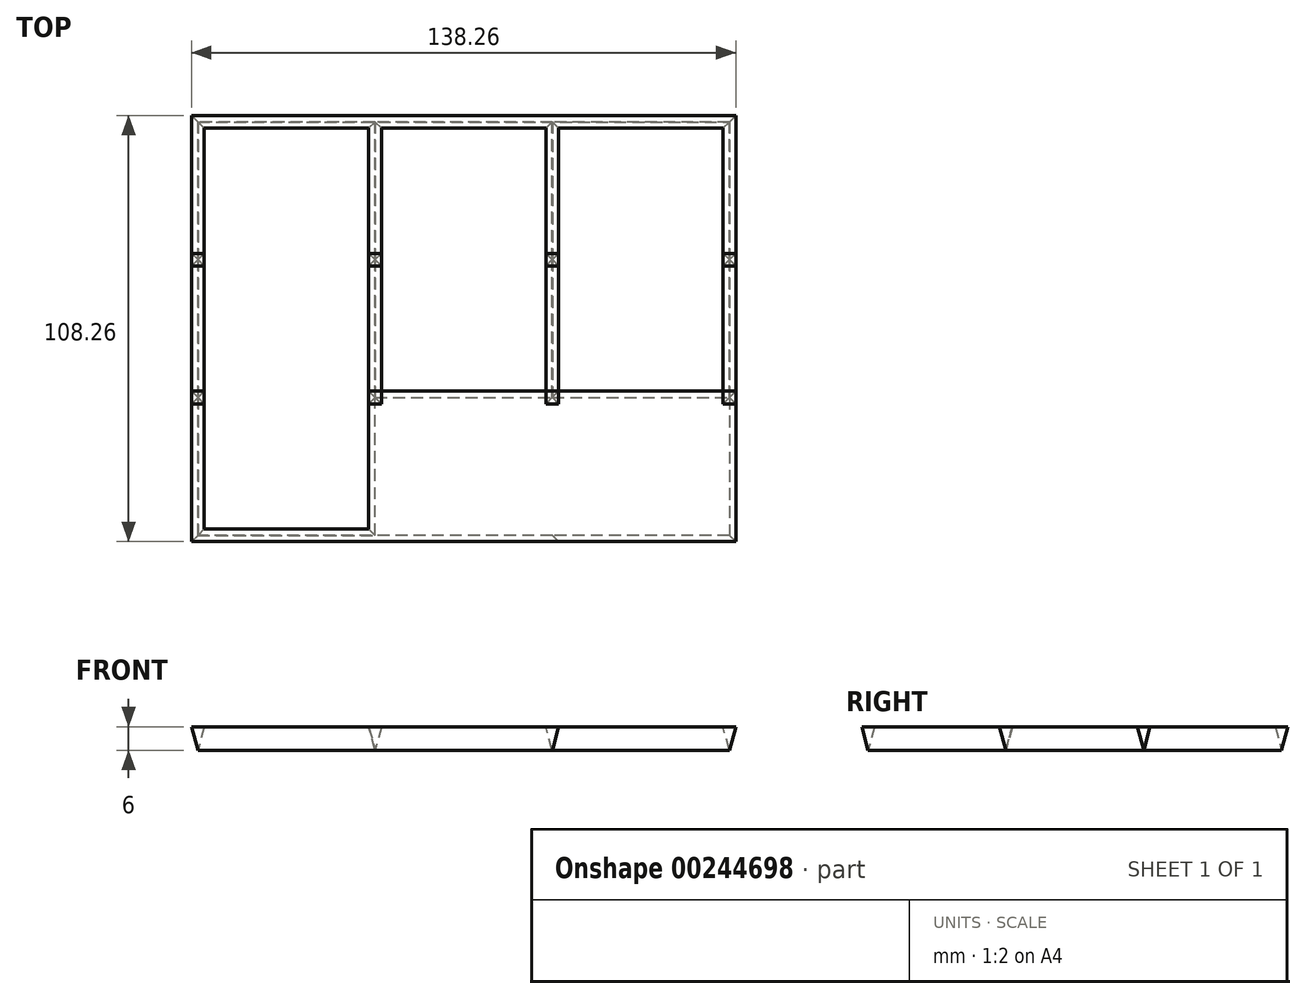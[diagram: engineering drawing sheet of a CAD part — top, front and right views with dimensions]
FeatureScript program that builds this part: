
annotation { "Feature Type Name" : "Feature", "Feature Type Description" : "" }
export const myFeature = defineFeature(function(context is Context, id is Id, definition is map)
    precondition{}
    {
        {
            var Q0;
            Q0=qCreatedBy(makeId("Top.planeOp"),FACE);
            var sketch = newSketch(context, id + "F0", { "sketchPlane" : qUnion([Q0])});
            skLineSegment(sketch, "E0.bottom", {"start": v(0, 0) * mm, "end": v(45, 0) * mm});
            skLineSegment(sketch, "E0.top", {"start": v(0, 35) * mm, "end": v(45, 35) * mm});
            skLineSegment(sketch, "E0.left", {"start": v(0, 0) * mm, "end": v(0, 35) * mm});
            skLineSegment(sketch, "E0.right", {"start": v(45, 0) * mm, "end": v(45, 35) * mm});
            skLineSegment(sketch, "E1.0", {"start": v(-0.01, 35.01) * mm, "end": v(45, 35.01) * mm});
            skLineSegment(sketch, "E1.1", {"start": v(-0.01, -0.01) * mm, "end": v(-0.01, 35.01) * mm});
            skLineSegment(sketch, "E1.2", {"start": v(-0.01, -0.01) * mm, "end": v(45, -0.01) * mm});
            skLineSegment(sketch, "E1.3", {"start": v(45, -0.01) * mm, "end": v(45, 35.01) * mm});
            skLineSegment(sketch, "E2.0.1.0", {"start": v(45, 35) * mm, "end": v(45, 70.02) * mm});
            skLineSegment(sketch, "E2.0.1.1", {"start": v(-0.01, 35) * mm, "end": v(45, 35) * mm});
            skLineSegment(sketch, "E2.0.1.2", {"start": v(-0.01, 35) * mm, "end": v(-0.01, 70.02) * mm});
            skLineSegment(sketch, "E2.0.1.3", {"start": v(-0.01, 70.02) * mm, "end": v(45, 70.02) * mm});
            skLineSegment(sketch, "E2.0.1.4", {"start": v(0, 70.01) * mm, "end": v(45, 70.01) * mm});
            skLineSegment(sketch, "E2.0.1.5", {"start": v(45, 35) * mm, "end": v(45, 70.01) * mm});
            skLineSegment(sketch, "E2.0.1.6", {"start": v(0, 35) * mm, "end": v(0, 70.01) * mm});
            skLineSegment(sketch, "E2.0.2.0", {"start": v(45, 70) * mm, "end": v(45, 105.03) * mm});
            skLineSegment(sketch, "E2.0.2.1", {"start": v(-0.01, 70) * mm, "end": v(45, 70) * mm});
            skLineSegment(sketch, "E2.0.2.2", {"start": v(-0.01, 70) * mm, "end": v(-0.01, 105.03) * mm});
            skLineSegment(sketch, "E2.0.2.3", {"start": v(-0.01, 105.03) * mm, "end": v(45, 105.03) * mm});
            skLineSegment(sketch, "E2.0.2.4", {"start": v(0, 105.02) * mm, "end": v(45, 105.02) * mm});
            skLineSegment(sketch, "E2.0.2.5", {"start": v(45, 70.02) * mm, "end": v(45, 105.02) * mm});
            skLineSegment(sketch, "E2.0.2.6", {"start": v(0, 70.02) * mm, "end": v(0, 105.02) * mm});
            skLineSegment(sketch, "E2.0.2.7", {"start": v(0, 70.02) * mm, "end": v(45, 70.02) * mm});
            skLineSegment(sketch, "E2.1.0.0", {"start": v(90.02, -0.01) * mm, "end": v(90.02, 35.01) * mm});
            skLineSegment(sketch, "E2.1.0.1", {"start": v(45, -0.01) * mm, "end": v(90.02, -0.01) * mm});
            skLineSegment(sketch, "E2.1.0.3", {"start": v(45, 35.01) * mm, "end": v(90.02, 35.01) * mm});
            skLineSegment(sketch, "E2.1.0.4", {"start": v(45, 35) * mm, "end": v(90.01, 35) * mm});
            skLineSegment(sketch, "E2.1.0.5", {"start": v(90.01, 0) * mm, "end": v(90.01, 35) * mm});
            skLineSegment(sketch, "E2.1.0.7", {"start": v(45, 0) * mm, "end": v(90.01, 0) * mm});
            skLineSegment(sketch, "E2.1.1.0", {"start": v(90.02, 35) * mm, "end": v(90.02, 70.02) * mm});
            skLineSegment(sketch, "E2.1.1.1", {"start": v(45, 35) * mm, "end": v(90.02, 35) * mm});
            skLineSegment(sketch, "E2.1.1.2", {"start": v(45, 35) * mm, "end": v(45, 70.02) * mm});
            skLineSegment(sketch, "E2.1.1.3", {"start": v(45, 70.02) * mm, "end": v(90.02, 70.02) * mm});
            skLineSegment(sketch, "E2.1.1.4", {"start": v(45, 70.01) * mm, "end": v(90.01, 70.01) * mm});
            skLineSegment(sketch, "E2.1.1.5", {"start": v(90.01, 35) * mm, "end": v(90.01, 70.01) * mm});
            skLineSegment(sketch, "E2.1.1.6", {"start": v(45, 35) * mm, "end": v(45, 70.01) * mm});
            skLineSegment(sketch, "E2.1.1.7", {"start": v(45, 35) * mm, "end": v(90.01, 35) * mm});
            skLineSegment(sketch, "E2.1.2.0", {"start": v(90.02, 70) * mm, "end": v(90.02, 105.03) * mm});
            skLineSegment(sketch, "E2.1.2.1", {"start": v(45, 70) * mm, "end": v(90.02, 70) * mm});
            skLineSegment(sketch, "E2.1.2.2", {"start": v(45, 70) * mm, "end": v(45, 105.03) * mm});
            skLineSegment(sketch, "E2.1.2.3", {"start": v(45, 105.03) * mm, "end": v(90.02, 105.03) * mm});
            skLineSegment(sketch, "E2.1.2.4", {"start": v(45, 105.02) * mm, "end": v(90.01, 105.02) * mm});
            skLineSegment(sketch, "E2.1.2.5", {"start": v(90.01, 70.02) * mm, "end": v(90.01, 105.02) * mm});
            skLineSegment(sketch, "E2.1.2.6", {"start": v(45, 70.02) * mm, "end": v(45, 105.02) * mm});
            skLineSegment(sketch, "E2.1.2.7", {"start": v(45, 70.02) * mm, "end": v(90.01, 70.02) * mm});
            skLineSegment(sketch, "E2.2.0.0", {"start": v(135.03, -0.01) * mm, "end": v(135.03, 35.01) * mm});
            skLineSegment(sketch, "E2.2.0.1", {"start": v(90, -0.01) * mm, "end": v(135.03, -0.01) * mm});
            skLineSegment(sketch, "E2.2.0.2", {"start": v(90.01, -0.01) * mm, "end": v(90.01, 35.01) * mm});
            skLineSegment(sketch, "E2.2.0.3", {"start": v(90.01, 35.01) * mm, "end": v(135.03, 35.01) * mm});
            skLineSegment(sketch, "E2.2.0.4", {"start": v(90.02, 35) * mm, "end": v(135.02, 35) * mm});
            skLineSegment(sketch, "E2.2.0.5", {"start": v(135.02, 0) * mm, "end": v(135.02, 35) * mm});
            skLineSegment(sketch, "E2.2.0.6", {"start": v(90.02, 0) * mm, "end": v(90.02, 35) * mm});
            skLineSegment(sketch, "E2.2.0.7", {"start": v(90.02, 0) * mm, "end": v(135.02, 0) * mm});
            skLineSegment(sketch, "E2.2.1.0", {"start": v(135.03, 35) * mm, "end": v(135.03, 70.02) * mm});
            skLineSegment(sketch, "E2.2.1.1", {"start": v(90, 35) * mm, "end": v(135.03, 35) * mm});
            skLineSegment(sketch, "E2.2.1.2", {"start": v(90.01, 35) * mm, "end": v(90.01, 70.02) * mm});
            skLineSegment(sketch, "E2.2.1.3", {"start": v(90.01, 70.02) * mm, "end": v(135.03, 70.02) * mm});
            skLineSegment(sketch, "E2.2.1.4", {"start": v(90.02, 70.01) * mm, "end": v(135.02, 70.01) * mm});
            skLineSegment(sketch, "E2.2.1.5", {"start": v(135.02, 35) * mm, "end": v(135.02, 70.01) * mm});
            skLineSegment(sketch, "E2.2.1.6", {"start": v(90.02, 35) * mm, "end": v(90.02, 70.01) * mm});
            skLineSegment(sketch, "E2.2.1.7", {"start": v(90.02, 35) * mm, "end": v(135.02, 35) * mm});
            skLineSegment(sketch, "E2.2.2.0", {"start": v(135.03, 70) * mm, "end": v(135.03, 105.03) * mm});
            skLineSegment(sketch, "E2.2.2.1", {"start": v(90, 70) * mm, "end": v(135.03, 70) * mm});
            skLineSegment(sketch, "E2.2.2.2", {"start": v(90.01, 70) * mm, "end": v(90.01, 105.03) * mm});
            skLineSegment(sketch, "E2.2.2.3", {"start": v(90.01, 105.03) * mm, "end": v(135.03, 105.03) * mm});
            skLineSegment(sketch, "E2.2.2.4", {"start": v(90.02, 105.02) * mm, "end": v(135.02, 105.02) * mm});
            skLineSegment(sketch, "E2.2.2.5", {"start": v(135.02, 70.02) * mm, "end": v(135.02, 105.02) * mm});
            skLineSegment(sketch, "E2.2.2.6", {"start": v(90.02, 70.02) * mm, "end": v(90.02, 105.02) * mm});
            skLineSegment(sketch, "E2.2.2.7", {"start": v(90.02, 70.02) * mm, "end": v(135.02, 70.02) * mm});
            skLineSegment(sketch, "E2.direction1", {"start": v(-0.01, -0.01) * mm, "end": v(45, -0.01) * mm, "construction": true});
            skLineSegment(sketch, "E2.direction2", {"start": v(-0.01, -0.01) * mm, "end": v(-0.01, 35) * mm, "construction": true});
            skSolve(sketch);
        }
        {
            var Q0;
            Q0=makeQuery(id+"F0.imprint","IMPRINT",FACE,{"disambiguationData":[TD([[makeQuery(id+"F0.imprint","IMPRINT",EDGE,{"derivedFrom":sQuery(id+"F0.wireOp",EDGE,"E2.1.2.4")}),1.0]])]});
            var Q1;
            {var subQ1=sQuery(id+"F0.wireOp",EDGE,"E2.1.0.0");Q1=makeQuery(id+"F0.imprint","IMPRINT",FACE,{"disambiguationData":[TD([[makeQuery(id+"F0.imprint","IMPRINT",EDGE,{"derivedFrom":subQ1}),-1.0]])]});}
            var Q2;
            {var subQ3=sQuery(id+"F0.wireOp",EDGE,"E2.0.2.3");Q2=makeQuery(id+"F0.imprint","IMPRINT",FACE,{"disambiguationData":[TD([[makeQuery(id+"F0.imprint","IMPRINT",EDGE,{"derivedFrom":subQ3}),-1.0]])]});}
            var Q3;
            {var subQ3=sQuery(id+"F0.wireOp",EDGE,"E2.0.1.6");Q3=makeQuery(id+"F0.imprint","IMPRINT",FACE,{"disambiguationData":[TD([[makeQuery(id+"F0.imprint","IMPRINT",EDGE,{"derivedFrom":subQ3}),1.0]])]});}
            var Q4;
            Q4=makeQuery(id+"F0.imprint","IMPRINT",FACE,{"disambiguationData":[TD([[makeQuery(id+"F0.imprint","IMPRINT",EDGE,{"derivedFrom":sQuery(id+"F0.wireOp",EDGE,"E0.bottom")}),-1.0]])]});
            var Q5;
            Q5=makeQuery(id+"F0.imprint","IMPRINT",FACE,{"disambiguationData":[TD([[makeQuery(id+"F0.imprint","IMPRINT",EDGE,{"derivedFrom":sQuery(id+"F0.wireOp",EDGE,"E2.2.2.4")}),1.0]])]});
            var Q6;
            {var subQ3=sQuery(id+"F0.wireOp",EDGE,"E2.2.1.5");Q6=makeQuery(id+"F0.imprint","IMPRINT",FACE,{"disambiguationData":[TD([[makeQuery(id+"F0.imprint","IMPRINT",EDGE,{"derivedFrom":subQ3}),-1.0]])]});}
            var Q7;
            {var subQ4=sQuery(id+"F0.wireOp",EDGE,"E1.3");Q7=makeQuery(id+"F0.imprint","IMPRINT",FACE,{"disambiguationData":[TD([[makeQuery(id+"F0.imprint","IMPRINT",EDGE,{"derivedFrom":subQ4}),-1.0]])]});}
            var Q8;
            {var subQ7=sQuery(id+"F0.wireOp",EDGE,"E0.top");Q8=makeQuery(id+"F0.imprint","IMPRINT",FACE,{"disambiguationData":[TD([[makeQuery(id+"F0.imprint","IMPRINT",EDGE,{"derivedFrom":subQ7}),-1.0]])]});}
            var Q9;
            {var subQ3=sQuery(id+"F0.wireOp",EDGE,"E2.1.1.5");Q9=makeQuery(id+"F0.imprint","IMPRINT",FACE,{"disambiguationData":[TD([[makeQuery(id+"F0.imprint","IMPRINT",EDGE,{"derivedFrom":subQ3}),-1.0]])]});}
            var Q10;
            {var subQ0=sQuery(id+"F0.wireOp",EDGE,"E2.1.0.0");Q10=makeQuery(id+"F0.imprint","IMPRINT",FACE,{"disambiguationData":[TD([[makeQuery(id+"F0.imprint","IMPRINT",EDGE,{"derivedFrom":subQ0}),1.0]])]});}
            var Q11;
            {var subQ0=sQuery(id+"F0.wireOp",EDGE,"E2.1.2.3");var subQ1=sQuery(id+"F0.wireOp",EDGE,"E2.0.2.0");var subQ2=makeQuery(id+"F0.imprint","INTERSECT",VERTEX,{"derivedFrom":[subQ1,subQ0]});Q11=makeQuery(id+"F0.imprint","IMPRINT",FACE,{"disambiguationData":[TD([[makeQuery(id+"F0.imprint","IMPRINT",EDGE,{"disambiguationData":[TD([[subQ2,1.0]])],"derivedFrom":subQ1}),1.0]])]});}
            var Q12;
            {var subQ0=sQuery(id+"F0.wireOp",EDGE,"E1.3");Q12=makeQuery(id+"F0.imprint","IMPRINT",FACE,{"disambiguationData":[TD([[makeQuery(id+"F0.imprint","IMPRINT",EDGE,{"derivedFrom":subQ0}),1.0]])]});}
            var Q13;
            {var subQ0=sQuery(id+"F0.wireOp",EDGE,"E2.2.2.3");var subQ1=sQuery(id+"F0.wireOp",EDGE,"E2.1.2.0");var subQ2=makeQuery(id+"F0.imprint","INTERSECT",VERTEX,{"derivedFrom":[subQ1,subQ0]});Q13=makeQuery(id+"F0.imprint","IMPRINT",FACE,{"disambiguationData":[TD([[makeQuery(id+"F0.imprint","IMPRINT",EDGE,{"disambiguationData":[TD([[subQ2,1.0]])],"derivedFrom":subQ1}),1.0]])]});}
            var Q14;
            {var subQ7=sQuery(id+"F0.wireOp",EDGE,"E2.1.2.7");Q14=makeQuery(id+"F0.imprint","IMPRINT",FACE,{"disambiguationData":[TD([[makeQuery(id+"F0.imprint","IMPRINT",EDGE,{"derivedFrom":subQ7}),-1.0]])]});}
            var Q15;
            {var subQ5=sQuery(id+"F0.wireOp",EDGE,"E2.1.1.6");Q15=makeQuery(id+"F0.imprint","IMPRINT",FACE,{"disambiguationData":[TD([[makeQuery(id+"F0.imprint","IMPRINT",EDGE,{"derivedFrom":subQ5}),1.0]])]});}
            var Q16;
            {var subQ7=sQuery(id+"F0.wireOp",EDGE,"E2.1.1.7");Q16=makeQuery(id+"F0.imprint","IMPRINT",FACE,{"disambiguationData":[TD([[makeQuery(id+"F0.imprint","IMPRINT",EDGE,{"derivedFrom":subQ7}),-1.0]])]});}
            var Q17;
            {var subQ1=sQuery(id+"F0.wireOp",EDGE,"E2.0.1.0");var subQ3=sQuery(id+"F0.wireOp",EDGE,"E2.1.0.3");var subQ4=makeQuery(id+"F0.imprint","INTERSECT",VERTEX,{"derivedFrom":[subQ1,subQ3]});Q17=makeQuery(id+"F0.imprint","IMPRINT",FACE,{"disambiguationData":[TD([[makeQuery(id+"F0.imprint","IMPRINT",EDGE,{"disambiguationData":[TD([[subQ4,-1.0]])],"derivedFrom":subQ1}),1.0]])]});}
            var Q18;
            {var subQ8=sQuery(id+"F0.wireOp",EDGE,"E2.2.2.7");Q18=makeQuery(id+"F0.imprint","IMPRINT",FACE,{"disambiguationData":[TD([[makeQuery(id+"F0.imprint","IMPRINT",EDGE,{"derivedFrom":subQ8}),-1.0]])]});}
            var Q19;
            {var subQ5=sQuery(id+"F0.wireOp",EDGE,"E2.2.1.7");Q19=makeQuery(id+"F0.imprint","IMPRINT",FACE,{"disambiguationData":[TD([[makeQuery(id+"F0.imprint","IMPRINT",EDGE,{"derivedFrom":subQ5}),-1.0]])]});}
            var Q20;
            {var subQ8=sQuery(id+"F0.wireOp",EDGE,"E2.0.2.7");Q20=makeQuery(id+"F0.imprint","IMPRINT",FACE,{"disambiguationData":[TD([[makeQuery(id+"F0.imprint","IMPRINT",EDGE,{"derivedFrom":subQ8}),-1.0]])]});}
            var Q21;
            {var subQ3=sQuery(id+"F0.wireOp",EDGE,"E2.0.1.5");Q21=makeQuery(id+"F0.imprint","IMPRINT",FACE,{"disambiguationData":[TD([[makeQuery(id+"F0.imprint","IMPRINT",EDGE,{"derivedFrom":subQ3}),-1.0]])]});}
            var Q22;
            {var subQ5=sQuery(id+"F0.wireOp",EDGE,"E2.2.1.6");Q22=makeQuery(id+"F0.imprint","IMPRINT",FACE,{"disambiguationData":[TD([[makeQuery(id+"F0.imprint","IMPRINT",EDGE,{"derivedFrom":subQ5}),1.0]])]});}
            var Q23;
            {var subQ1=sQuery(id+"F0.wireOp",EDGE,"E2.1.1.0");var subQ3=sQuery(id+"F0.wireOp",EDGE,"E2.2.0.3");var subQ4=makeQuery(id+"F0.imprint","INTERSECT",VERTEX,{"derivedFrom":[subQ1,subQ3]});Q23=makeQuery(id+"F0.imprint","IMPRINT",FACE,{"disambiguationData":[TD([[makeQuery(id+"F0.imprint","IMPRINT",EDGE,{"disambiguationData":[TD([[subQ4,-1.0]])],"derivedFrom":subQ1}),1.0]])]});}
            var Q24;
            {var subQ1=sQuery(id+"F0.wireOp",EDGE,"E2.1.1.0");var subQ3=sQuery(id+"F0.wireOp",EDGE,"E2.2.0.3");var subQ4=makeQuery(id+"F0.imprint","INTERSECT",VERTEX,{"derivedFrom":[subQ1,subQ3]});Q24=makeQuery(id+"F0.imprint","IMPRINT",FACE,{"disambiguationData":[TD([[makeQuery(id+"F0.imprint","IMPRINT",EDGE,{"disambiguationData":[TD([[subQ4,1.0]])],"derivedFrom":subQ1}),1.0]])]});}
            var Q25;
            {var subQ1=sQuery(id+"F0.wireOp",EDGE,"E2.0.2.0");var subQ3=sQuery(id+"F0.wireOp",EDGE,"E2.1.1.3");var subQ4=makeQuery(id+"F0.imprint","INTERSECT",VERTEX,{"derivedFrom":[subQ1,subQ3]});Q25=makeQuery(id+"F0.imprint","IMPRINT",FACE,{"disambiguationData":[TD([[makeQuery(id+"F0.imprint","IMPRINT",EDGE,{"disambiguationData":[TD([[subQ4,1.0]])],"derivedFrom":subQ1}),1.0]])]});}
            var Q26;
            {var subQ1=sQuery(id+"F0.wireOp",EDGE,"E2.0.1.0");var subQ3=sQuery(id+"F0.wireOp",EDGE,"E2.1.0.3");var subQ4=makeQuery(id+"F0.imprint","INTERSECT",VERTEX,{"derivedFrom":[subQ1,subQ3]});Q26=makeQuery(id+"F0.imprint","IMPRINT",FACE,{"disambiguationData":[TD([[makeQuery(id+"F0.imprint","IMPRINT",EDGE,{"disambiguationData":[TD([[subQ4,1.0]])],"derivedFrom":subQ1}),1.0]])]});}
            var Q27;
            {var subQ1=sQuery(id+"F0.wireOp",EDGE,"E2.1.2.0");var subQ3=sQuery(id+"F0.wireOp",EDGE,"E2.2.1.3");var subQ4=makeQuery(id+"F0.imprint","INTERSECT",VERTEX,{"derivedFrom":[subQ1,subQ3]});Q27=makeQuery(id+"F0.imprint","IMPRINT",FACE,{"disambiguationData":[TD([[makeQuery(id+"F0.imprint","IMPRINT",EDGE,{"disambiguationData":[TD([[subQ4,1.0]])],"derivedFrom":subQ1}),1.0]])]});}
            extrude(context, id + "F1", {"entities" : qUnion([Q0, Q1, Q2, Q3, Q4, Q5, Q6, Q7, Q8, Q9, Q10, Q11, Q12, Q13, Q14, Q15, Q16, Q17, Q18, Q19, Q20, Q21, Q22, Q23, Q24, Q25, Q26, Q27]), "depth" : 6 * mm, "hasDraft" : true, "draftAngle" : 15 * degree});
        }
    });
